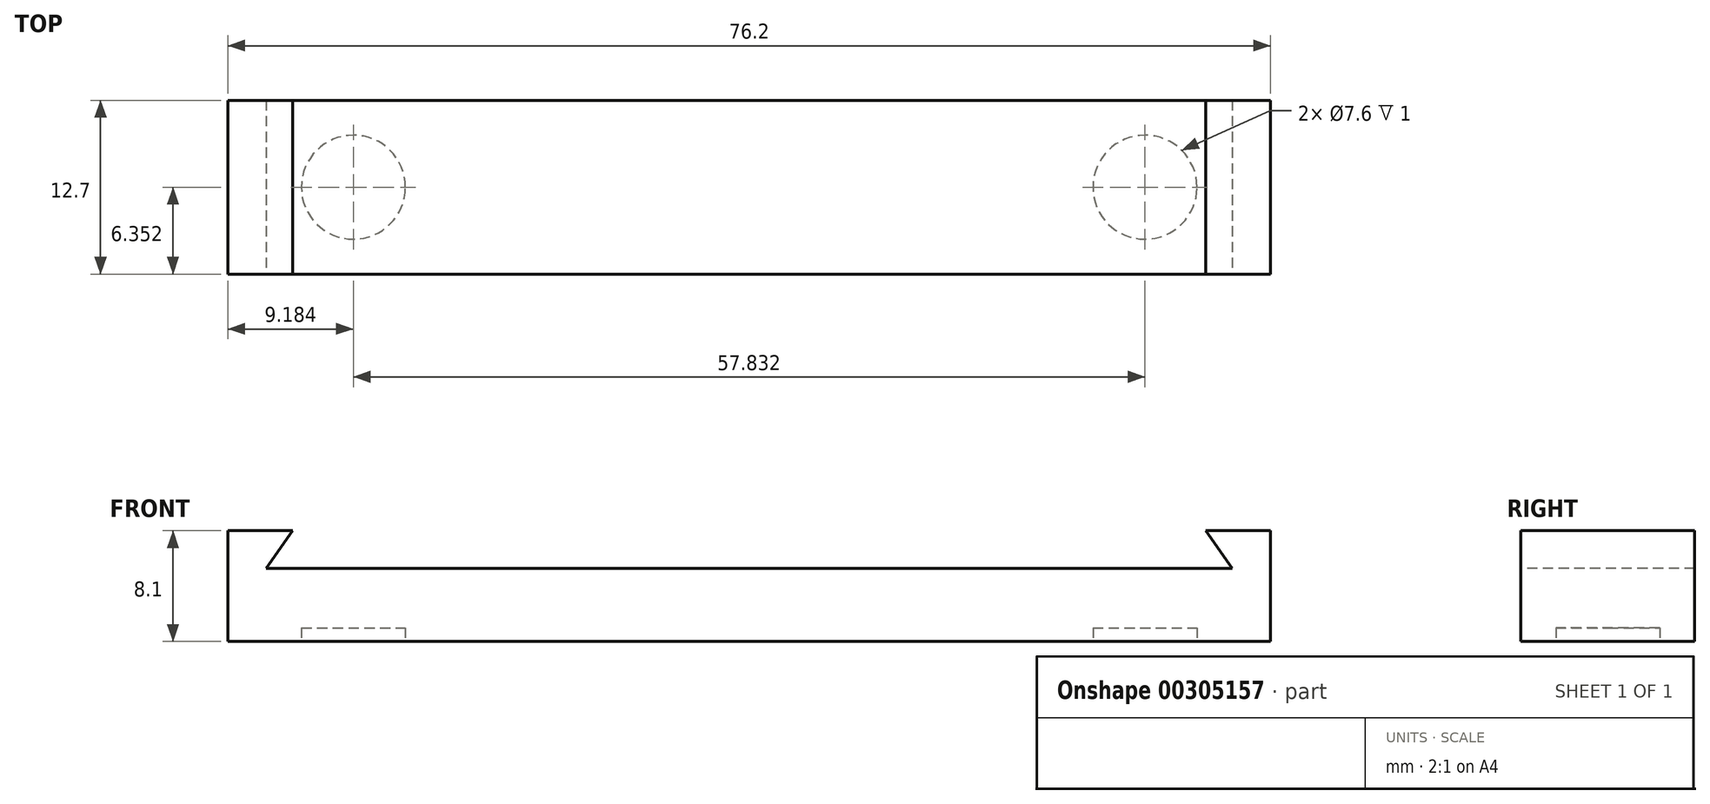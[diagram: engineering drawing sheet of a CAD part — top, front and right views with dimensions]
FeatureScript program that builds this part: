
annotation { "Feature Type Name" : "Feature", "Feature Type Description" : "" }
export const myFeature = defineFeature(function(context is Context, id is Id, definition is map)
    precondition{}
    {
        {
            var Q0;
            Q0=qCreatedBy(makeId("Top.planeOp"),FACE);
            var sketch = newSketch(context, id + "F0", { "sketchPlane" : qUnion([Q0])});
            skLineSegment(sketch, "E0.bottom", {"start": v(-40.74, 3.7) * mm, "end": v(35.46, 3.7) * mm});
            skLineSegment(sketch, "E0.top", {"start": v(-40.74, -9) * mm, "end": v(35.46, -9) * mm});
            skLineSegment(sketch, "E0.left", {"start": v(-40.74, 3.7) * mm, "end": v(-40.74, -9) * mm});
            skLineSegment(sketch, "E0.right", {"start": v(35.46, 3.7) * mm, "end": v(35.46, -9) * mm});
            skSolve(sketch);
        }
        {
            var Q0;
            Q0 = qSketchRegion(id + "F0", true);
            extrude(context, id + "F1", {"entities" : qUnion([Q0]), "depth" : 5.33 * mm});
        }
        {
            var Q0;
            Q0=makeQuery(id+"F1.opExtrude","SWEPT_FACE",FACE,{"disambiguationData":[OSD([sQuery(id+"F0.wireOp",EDGE,"E0.top")])]});
            var sketch = newSketch(context, id + "F2", { "sketchPlane" : qUnion([Q0])});
            skLineSegment(sketch, "E1", {"start": v(-37.92, 5.33) * mm, "end": v(-35.99, 8.1) * mm});
            skLineSegment(sketch, "E2", {"start": v(-35.99, 8.1) * mm, "end": v(-40.74, 8.1) * mm});
            skLineSegment(sketch, "E3", {"start": v(-40.74, 8.1) * mm, "end": v(-40.74, 5.33) * mm});
            skLineSegment(sketch, "E4", {"start": v(-2.64, 5.33) * mm, "end": v(-2.64, 10.35) * mm, "construction": true});
            skPoint(sketch, "E4.endSnap0", {"position": v(-2.64, 5.33) * mm});
            skLineSegment(sketch, "E5.MirrorCS", {"start": v(35.46, 8.1) * mm, "end": v(35.46, 5.33) * mm});
            skLineSegment(sketch, "E6.MirrorCS", {"start": v(32.64, 5.33) * mm, "end": v(30.7, 8.1) * mm});
            skLineSegment(sketch, "E7.MirrorCS", {"start": v(30.7, 8.1) * mm, "end": v(35.46, 8.1) * mm});
            skSolve(sketch);
        }
        {
            var Q0;
            {var subQ0=sQuery(id+"F2.wireOp",EDGE,"E1");Q0=makeQuery(id+"F2.imprint","IMPRINT",FACE,{"disambiguationData":[TD([[makeQuery(id+"F2.imprint","IMPRINT",EDGE,{"derivedFrom":subQ0}),1.0]])]});}
            var Q1;
            {var subQ0=sQuery(id+"F2.wireOp",EDGE,"E5.MirrorCS");Q1=makeQuery(id+"F2.imprint","IMPRINT",FACE,{"disambiguationData":[TD([[makeQuery(id+"F2.imprint","IMPRINT",EDGE,{"derivedFrom":subQ0}),-1.0]])]});}
            var Q2;
            Q2=makeQuery(id+"F1.opExtrude","SWEPT_FACE",FACE,{"disambiguationData":[OSD([sQuery(id+"F0.wireOp",EDGE,"E0.bottom")])]});
            extrude(context, id + "F3", {"entities" : qUnion([Q0, Q1]), "operationType" : NewBodyOperationType.ADD, "endBound" : BoundingType.UP_TO_SURFACE, "oppositeDirection" : true, "endBoundEntityFace" : qUnion([Q2]), "depth" : 25.4 * mm});
        }
        {
            var Q0;
            Q0=makeQuery(id+"F1.opExtrude","CAP_FACE",FACE,{"disambiguationData":[OSD([sQuery(id+"F0.wireOp",EDGE,"E0.bottom"),sQuery(id+"F0.wireOp",EDGE,"E0.top"),sQuery(id+"F0.wireOp",EDGE,"E0.left"),sQuery(id+"F0.wireOp",EDGE,"E0.right")])],"isStart":true});
            var sketch = newSketch(context, id + "F4", { "sketchPlane" : qUnion([Q0])});
            skCircle(sketch, "E8", {"center": v(-31.56, 2.65) * mm, "radius": 3.8 * mm});
            skPoint(sketch, "E8.centerSnap0", {"position": v(-40.74, 2.65) * mm});
            skLineSegment(sketch, "E9", {"start": v(-2.64, 9) * mm, "end": v(-2.64, 5.15) * mm, "construction": true});
            skCircle(sketch, "E10.MirrorC", {"center": v(26.28, 2.65) * mm, "radius": 3.8 * mm});
            skSolve(sketch);
        }
        {
            var Q0;
            Q0 = qSketchRegion(id + "F4", true);
            extrude(context, id + "F5", {"entities" : qUnion([Q0]), "operationType" : NewBodyOperationType.REMOVE, "oppositeDirection" : true, "depth" : 1 * mm});
        }
    });
